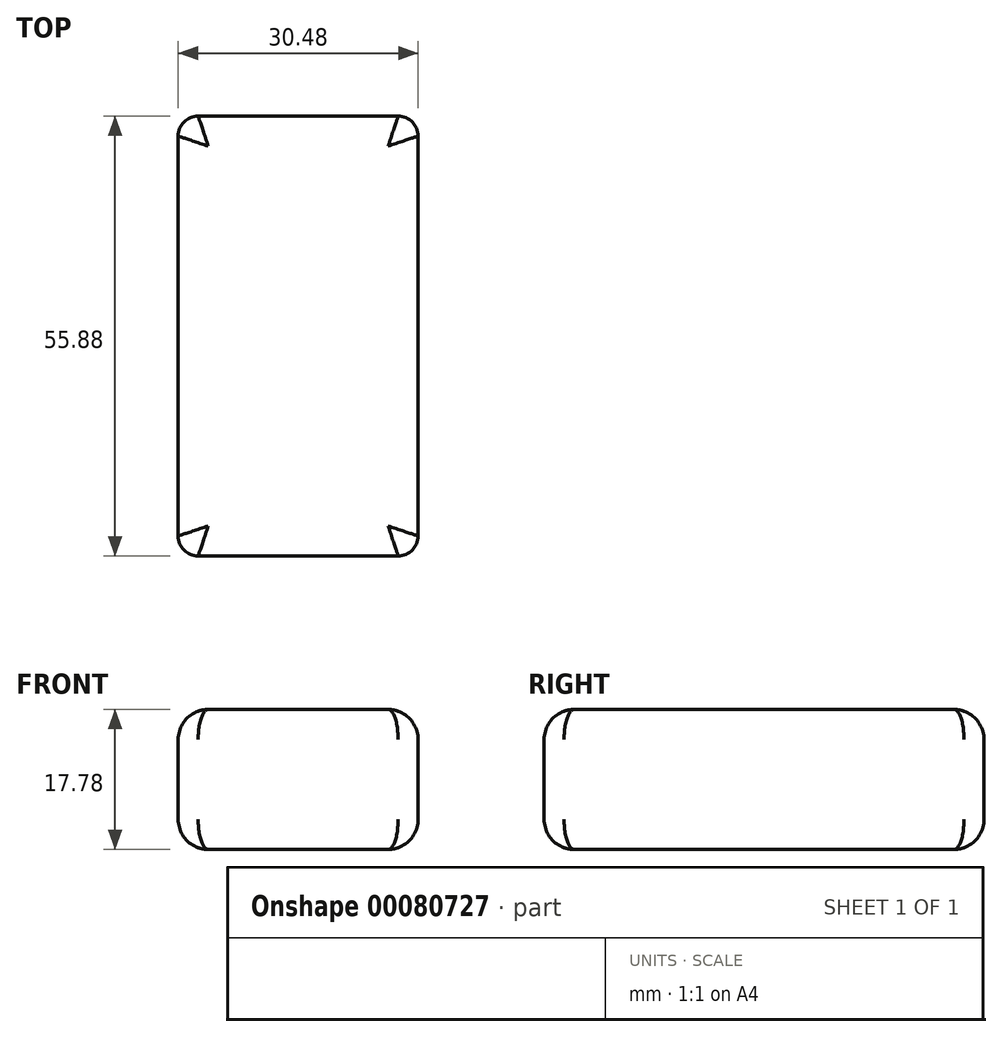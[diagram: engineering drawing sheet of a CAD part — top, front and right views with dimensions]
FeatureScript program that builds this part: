
annotation { "Feature Type Name" : "Feature", "Feature Type Description" : "" }
export const myFeature = defineFeature(function(context is Context, id is Id, definition is map)
    precondition{}
    {
        {
            var Q0;
            Q0=qCreatedBy(makeId("Top.planeOp"),FACE);
            var sketch = newSketch(context, id + "F0", { "sketchPlane" : qUnion([Q0])});
            skLineSegment(sketch, "E0.bottom", {"start": v(15.24, -27.94) * mm, "end": v(-15.24, -27.94) * mm});
            skLineSegment(sketch, "E0.top", {"start": v(15.24, 27.94) * mm, "end": v(-15.24, 27.94) * mm});
            skLineSegment(sketch, "E0.left", {"start": v(15.24, -27.94) * mm, "end": v(15.24, 27.94) * mm});
            skLineSegment(sketch, "E0.right", {"start": v(-15.24, -27.94) * mm, "end": v(-15.24, 27.94) * mm});
            skPoint(sketch, "E0.middle", {"position": v(0, 0) * mm});
            skSolve(sketch);
        }
        {
            var Q0;
            Q0=makeQuery(id+"F0.imprint","IMPRINT",FACE,{"disambiguationData":[TD([[makeQuery(id+"F0.imprint","IMPRINT",EDGE,{"derivedFrom":sQuery(id+"F0.wireOp",EDGE,"E0.bottom")}),-1.0]])]});
            extrude(context, id + "F1", {"entities" : qUnion([Q0]), "depth" : 17.78 * mm});
        }
        {
            var Q0;
            Q0=makeQuery(id+"F1.opExtrude","CAP_EDGE",EDGE,{"disambiguationData":[OSD([sQuery(id+"F0.wireOp",EDGE,"E0.right")])],"isStart":false});
            var Q1;
            Q1=makeQuery(id+"F1.opExtrude","CAP_EDGE",EDGE,{"disambiguationData":[OSD([sQuery(id+"F0.wireOp",EDGE,"E0.bottom")])],"isStart":false});
            var Q2;
            Q2=makeQuery(id+"F1.opExtrude","CAP_EDGE",EDGE,{"disambiguationData":[OSD([sQuery(id+"F0.wireOp",EDGE,"E0.left")])],"isStart":false});
            var Q3;
            Q3=makeQuery(id+"F1.opExtrude","CAP_EDGE",EDGE,{"disambiguationData":[OSD([sQuery(id+"F0.wireOp",EDGE,"E0.top")])],"isStart":false});
            var Q4;
            Q4=makeQuery(id+"F1.opExtrude","CAP_EDGE",EDGE,{"disambiguationData":[OSD([sQuery(id+"F0.wireOp",EDGE,"E0.right")])],"isStart":true});
            var Q5;
            Q5=makeQuery(id+"F1.opExtrude","CAP_EDGE",EDGE,{"disambiguationData":[OSD([sQuery(id+"F0.wireOp",EDGE,"E0.bottom")])],"isStart":true});
            var Q6;
            Q6=makeQuery(id+"F1.opExtrude","CAP_EDGE",EDGE,{"disambiguationData":[OSD([sQuery(id+"F0.wireOp",EDGE,"E0.left")])],"isStart":true});
            var Q7;
            Q7=makeQuery(id+"F1.opExtrude","CAP_EDGE",EDGE,{"disambiguationData":[OSD([sQuery(id+"F0.wireOp",EDGE,"E0.top")])],"isStart":true});
            fillet(context, id + "F2", {"entities" : qUnion([Q0, Q1, Q2, Q3, Q4, Q5, Q6, Q7]), "radius" : 3.8 * mm, "tangentPropagation" : true, "allowEdgeOverflow" : false});
        }
        {
            var Q0;
            Q0=makeQuery(id+"F1.opExtrude","SWEPT_EDGE",EDGE,{"disambiguationData":[OSD([sQuery(id+"F0.wireOp",EDGE,"E0.bottom"),sQuery(id+"F0.wireOp",EDGE,"E0.right")])]});
            var Q1;
            Q1=makeQuery(id+"F1.opExtrude","SWEPT_EDGE",EDGE,{"disambiguationData":[OSD([sQuery(id+"F0.wireOp",EDGE,"E0.top"),sQuery(id+"F0.wireOp",EDGE,"E0.right")])]});
            var Q2;
            Q2=makeQuery(id+"F1.opExtrude","SWEPT_EDGE",EDGE,{"disambiguationData":[OSD([sQuery(id+"F0.wireOp",EDGE,"E0.top"),sQuery(id+"F0.wireOp",EDGE,"E0.left")])]});
            var Q3;
            Q3=makeQuery(id+"F1.opExtrude","SWEPT_EDGE",EDGE,{"disambiguationData":[OSD([sQuery(id+"F0.wireOp",EDGE,"E0.bottom"),sQuery(id+"F0.wireOp",EDGE,"E0.left")])]});
            fillet(context, id + "F3", {"entities" : qUnion([Q0, Q1, Q2, Q3]), "radius" : 2.54 * mm, "tangentPropagation" : true, "allowEdgeOverflow" : false});
        }
    });
